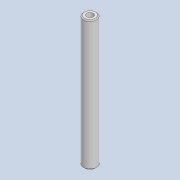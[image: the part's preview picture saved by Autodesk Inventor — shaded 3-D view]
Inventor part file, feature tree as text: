
AUTODESK INVENTOR PART (.ipt)
format: ipt  version: 2020 (Build 240168000, 168)  size: 81,920 bytes
history: native  units: mm
features: extrude x2, sketch x2, chamfer x1
ambient origin geometry x8: Origin, YZ Plane, XZ Plane, XY Plane, X Axis, Y Axis, Z Axis, Center Point
bodies: Solid1 (feature_tree)
feature tree (5):
  extrude  "Extrusion1"  Depth=30.0mm TaperAngle=0.0deg
  chamfer  "Chamfer1"  Distance=0.25mm Angle=45.0deg
  extrude  "Extrusion2"  Depth=30.0mm TaperAngle=0.0deg
  sketch  "Sketch1"  dims[d0=3.0mm d1=30.0mm d2=0.0mm d3=0.25mm d4=2.0mm d5=45.0deg]
  sketch  "Sketch2"  dims[d6=1.5mm d7=30.0mm d8=0.0mm]
